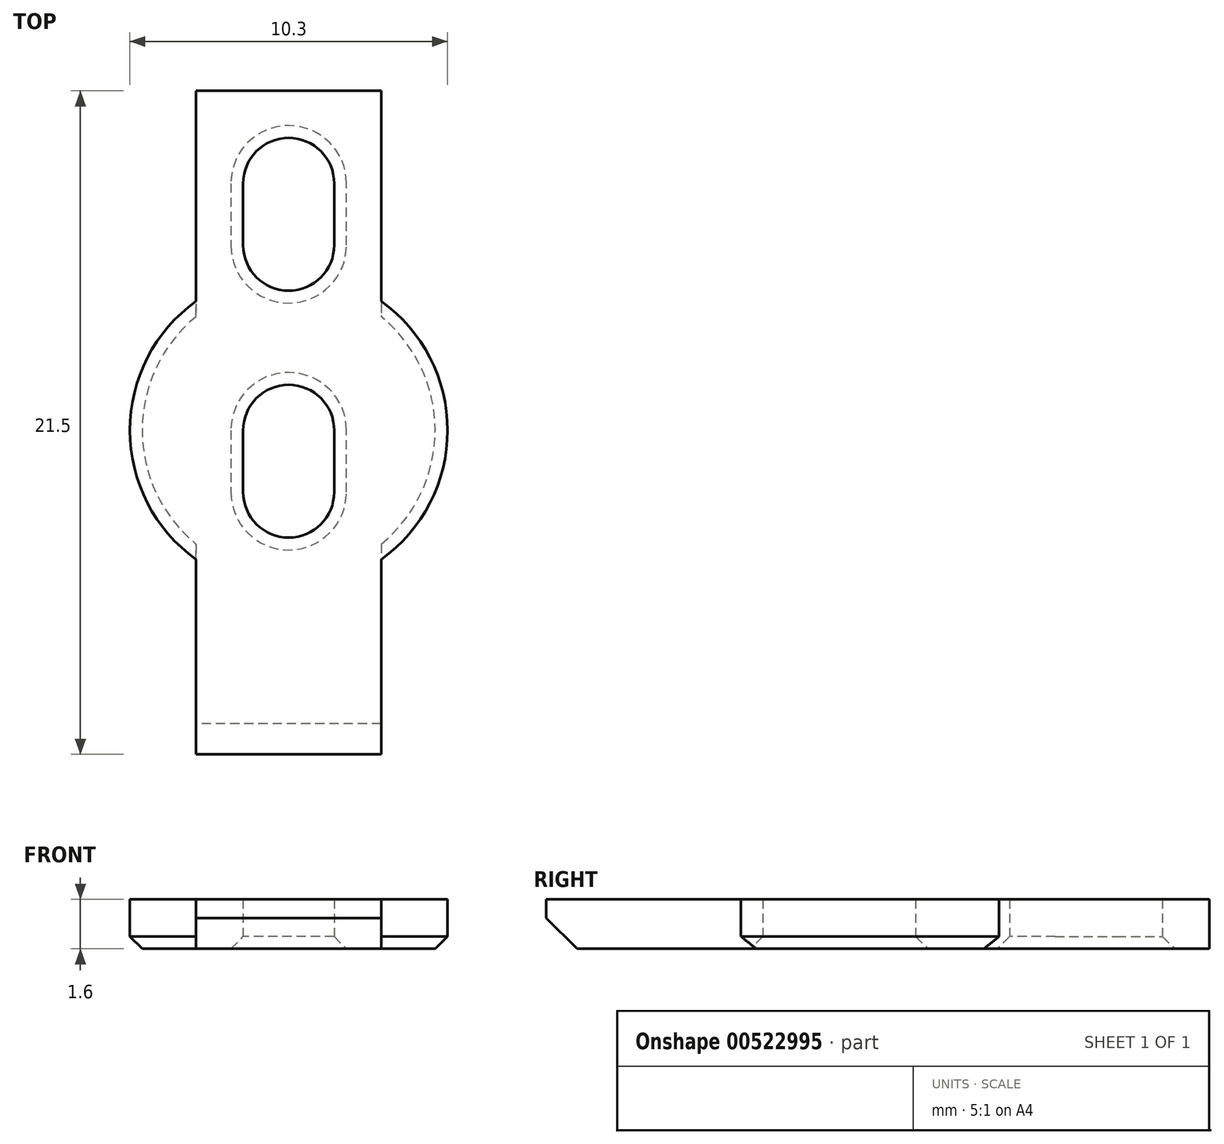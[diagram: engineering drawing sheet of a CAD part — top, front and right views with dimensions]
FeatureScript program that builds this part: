
annotation { "Feature Type Name" : "Feature", "Feature Type Description" : "" }
export const myFeature = defineFeature(function(context is Context, id is Id, definition is map)
    precondition{}
    {
        {
            var Q0;
            Q0=qCreatedBy(makeId("Top.planeOp"),FACE);
            var sketch = newSketch(context, id + "F0", { "sketchPlane" : qUnion([Q0])});
            skCircle(sketch, "E0", {"center": v(0, 0) * mm, "radius": 5.15 * mm});
            skLineSegment(sketch, "E1.bottom", {"start": v(-3, 11) * mm, "end": v(3, 11) * mm});
            skLineSegment(sketch, "E1.top", {"start": v(-3, -10.5) * mm, "end": v(3, -10.5) * mm});
            skLineSegment(sketch, "E1.left", {"start": v(-3, 11) * mm, "end": v(-3, -10.5) * mm});
            skLineSegment(sketch, "E1.right", {"start": v(3, 11) * mm, "end": v(3, -10.5) * mm});
            skLineSegment(sketch, "E2", {"start": v(0, 11) * mm, "end": v(0, 7) * mm, "construction": true});
            skLineSegment(sketch, "E3", {"start": v(0, 7) * mm, "end": v(0, -1) * mm, "construction": true});
            skLineSegment(sketch, "E4", {"start": v(0, -1) * mm, "end": v(0, -10.5) * mm, "construction": true});
            skArc(sketch, "E5", {"start": v(1.48, 0) * mm, "mid": v(0, 1.48) * mm, "end": v(-1.48, 0) * mm});
            skArc(sketch, "E6", {"start": v(-1.48, -2) * mm, "mid": v(0, -3.48) * mm, "end": v(1.48, -2) * mm});
            skLineSegment(sketch, "E7", {"start": v(-1.47, 0) * mm, "end": v(-1.47, -2) * mm});
            skLineSegment(sketch, "E8", {"start": v(1.48, 0) * mm, "end": v(1.48, -2) * mm});
            skLineSegment(sketch, "E9", {"start": v(1.48, -1) * mm, "end": v(0, -1) * mm, "construction": true});
            skArc(sketch, "E10", {"start": v(1.48, 8) * mm, "mid": v(0, 9.48) * mm, "end": v(-1.48, 8) * mm});
            skArc(sketch, "E11", {"start": v(-1.48, 6) * mm, "mid": v(0, 4.52) * mm, "end": v(1.48, 6) * mm});
            skLineSegment(sketch, "E12", {"start": v(1.48, 8) * mm, "end": v(1.48, 6) * mm});
            skLineSegment(sketch, "E13", {"start": v(-1.48, 8) * mm, "end": v(-1.48, 6) * mm});
            skLineSegment(sketch, "E14", {"start": v(0, 7) * mm, "end": v(1.48, 7) * mm, "construction": true});
            skSolve(sketch);
        }
        {
            var Q0;
            Q0=qSketchRegion(id+"F0",true);
            extrude(context, id + "F1", {"entities" : qUnion([Q0]), "depth" : 1.6 * mm});
        }
        {
            var Q0;
            {var subQ0=sQuery(id+"F0.wireOp",EDGE,"E1.left");var subQ1=sQuery(id+"F0.wireOp",EDGE,"E0");Q0=makeQuery(id+"F1.opExtrude","CAP_EDGE",EDGE,{"disambiguationData":[OSD([subQ1]),TDD([makeQuery(id+"F0.imprint","IMPRINT",EDGE,{"disambiguationData":[TD([[makeQuery(id+"F0.imprint","INTERSECT",VERTEX,{"disambiguationData":[OD(0.0)],"derivedFrom":[subQ1,subQ0]}),-1.0]])],"derivedFrom":subQ1})])],"isStart":true});}
            var Q1;
            {var subQ0=sQuery(id+"F0.wireOp",EDGE,"E1.right");var subQ1=sQuery(id+"F0.wireOp",EDGE,"E0");Q1=makeQuery(id+"F1.opExtrude","CAP_EDGE",EDGE,{"disambiguationData":[OSD([subQ1]),TDD([makeQuery(id+"F0.imprint","IMPRINT",EDGE,{"disambiguationData":[TD([[makeQuery(id+"F0.imprint","INTERSECT",VERTEX,{"disambiguationData":[OD(0.0)],"derivedFrom":[subQ1,subQ0]}),1.0]])],"derivedFrom":subQ1})])],"isStart":true});}
            var Q2;
            Q2=makeQuery(id+"F1.opExtrude","CAP_EDGE",EDGE,{"disambiguationData":[OSD([sQuery(id+"F0.wireOp",EDGE,"E8")])],"isStart":true});
            var Q3;
            Q3=makeQuery(id+"F1.opExtrude","CAP_EDGE",EDGE,{"disambiguationData":[OSD([sQuery(id+"F0.wireOp",EDGE,"E12")])],"isStart":true});
            chamfer(context, id + "F2", {"entities" : qUnion([Q0, Q1, Q2, Q3]), "width" : 0.4 * mm, "tangentPropagation" : true});
        }
        {
            var Q0;
            Q0=makeQuery(id+"F1.opExtrude","CAP_EDGE",EDGE,{"disambiguationData":[OSD([sQuery(id+"F0.wireOp",EDGE,"E1.top")])],"isStart":true});
            chamfer(context, id + "F3", {"entities" : qUnion([Q0]), "width" : 1 * mm, "tangentPropagation" : true});
        }
    });
